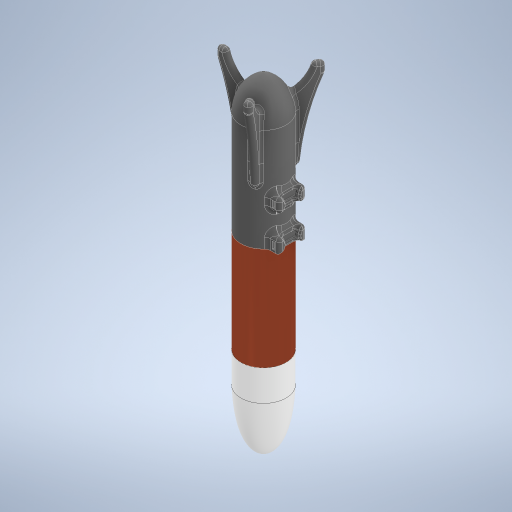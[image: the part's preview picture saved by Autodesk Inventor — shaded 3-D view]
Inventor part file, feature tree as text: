
AUTODESK INVENTOR PART (.ipt)
format: ipt  version: 2023 (Build 270158030, 158C)  size: 1,832,448 bytes
history: native  units: mm
features: fillet x17, sketch x15, extrude x14, other x12, plane x4, revolve x3, pattern_circular x2, pattern_linear x1, mirror x1, chamfer x1
ambient origin geometry x8: Origin, YZ Plane, XZ Plane, XY Plane, X Axis, Y Axis, Z Axis, Center Point
bodies: Body1 (feature_tree), Body2 (feature_tree), Body3 (feature_tree), Body4 (feature_tree), Body5 (feature_tree), Body6 (feature_tree), Body7 (feature_tree)
feature tree (70):
  other  "stage-one"
  extrude  "body-tube"  Depth=3.0mm
  extrude  "Extrusion2"  Depth=20.0mm
  extrude  "Extrusion3"  Depth=10.0mm
  plane  "Work Plane2"
  plane  "Work Plane4"
  extrude  "Extrusion4"  Depth=12.5mm
  plane  "Work Plane6"
  pattern_linear  "Rectangular Pattern1"  Count1=2  [1 undecoded]
  extrude  "Extrusion7"  Depth=6.0mm
  other  "Work Point2"
  revolve  "Revolution2"  [1 undecoded]
  mirror  "Mirror1"
  extrude  "Extrusion5"  Depth=4.0mm
  fillet  "Fillet1"  [1 undecoded]
  fillet  "Fillet2"  Radius=30.0mm
  fillet  "Fillet3"  Radius=200.0mm
  chamfer  "Chamfer1"  Distance=20.0mm
  fillet  "Fillet4"  Radius=7.0mm
  fillet  "Fillet5"  Radius=7.0mm
  fillet  "Fillet6"  Radius=5.0mm
  extrude  "Extrusion6"  Depth=2.0mm TaperAngle=45.0deg
  extrude  "fin 1 extrude"  Depth=5.0mm
  pattern_circular  "Circular Pattern1"  [2 undecoded]
  fillet  "Fillet7"  Radius=8.0mm
  fillet  "Fillet9"  Radius=10.0mm
  fillet  "Fillet10"  Radius=3.5mm
  fillet  "Fillet11"  [1 undecoded]
  fillet  "Fillet12"  Radius=1.0mm
  fillet  "Fillet13"  Radius=50.0mm
  extrude  "Extrusion9"  Depth=200.0mm
  extrude  "Extrusion10"  TaperAngle=90.0deg  [1 undecoded]
  extrude  "Extrusion11"  Depth=48.0mm
  extrude  "Extrusion12"  Depth=5.0mm
  other  "Work Point3"
  fillet  "Fillet15"  Radius=65.0mm
  fillet  "Fillet16"  Radius=15.0mm
  plane  "Work Plane7"
  extrude  "Extrusion14"  Depth=5.0mm
  revolve  "Revolution4"  [1 undecoded]
  fillet  "Fillet18"  Radius=126.0mm
  fillet  "Fillet19"  Radius=404.0mm
  fillet  "Fillet20"  Radius=150.0mm
  pattern_circular  "Circular Pattern2"  [2 undecoded]
  revolve  "Revolution3"  [1 undecoded]
  extrude  "Extrusion13"  Depth=5.0mm
  sketch  "Sketch1"  dims[d0=60.0mm d1=3.0mm]
  other  "rail-clamp-A"
  sketch  "Sketch5"  dims[d2=150.0mm d3=0.0mm d19=20.0mm]
  sketch  "Sketch6"  dims[d20=20.0mm d22=10.0mm]
  other  "Holding Bar"
  sketch  "Sketch8"  dims[d23=20.0mm d24=0.0mm d26=12.5mm]
  other  "bar-vertical"
  other  "Pattern of Holding Bar:1"
  other  "bar-angled"
  sketch  "Sketch9"  dims[d27=12.5mm]
  sketch  "Sketch10"  dims[d28=15.0mm]
  sketch  "Sketch11"  dims[d29=17.0mm]
  sketch  "Sketch12"  dims[d30=17.0mm]
  sketch  "Sketch13"  dims[d31=3.490659mm]
  sketch  "Sketch14"  dims[d33=3.490659mm]
  other  "stage-two"
  sketch  "Sketch15"  dims[d34=53.0mm d35=20.0mm]
  sketch  "Sketch16"  dims[d36=6.0mm d37=6.0mm]
  sketch  "Sketch17"  dims[d38=7.5mm d39=0.0mm d40=30.0mm]
  other  "nose-cone"
  sketch  "Sketch19"  dims[d41=53.296162mm d42=4.0mm]
  other  "drumsticks"
  sketch  "Sketch20"  dims[d43=200.0mm d44=100.0mm d45=0.0mm d46=0.0mm d47=90.0deg d49=30.0mm d50=200.0mm d51=100.0mm d52=0.0mm d53=0.0mm d56=20.0mm d58=50.0mm d59=7.0mm d60=7.0mm d61=5.0mm d62=2.0mm d63=2.0mm d64=45.0deg d65=5.0mm d66=5.0mm d67=8.0mm d68=10.0mm d70=3.5mm d76=0.0mm d77=0.0mm d78=1.0mm d79=50.0mm d80=0.0mm d85=53.0mm d86=52.992097mm d88=3.0mm d89=3.0mm d90=54.0mm d91=200.0mm d92=90.0deg d93=48.0mm d94=5.0mm d95=65.0mm d96=15.0mm d97=5.0mm d98=367.0mm d99=126.0mm d100=404.0mm d101=150.0mm d102=10.0mm d103=0.0mm d104=5.0mm d106=5.0mm d107=30.0mm d108=360.0deg d110=5.0mm d111=5.0mm d112=5.0mm d113=5.0mm d115=3.0mm d116=1.5mm d117=50.0mm d118=0.0mm d119=150.0mm d120=0.0mm d121=1.5mm d122=49.0mm d123=0.0mm d124=1.5mm d125=30.0mm d126=0.0mm d131=360.0deg d132=1.5mm d133=25.0mm d134=0.0mm d135=3.0mm d136=2.5mm d137=10.0mm d138=2.0mm d139=1.5mm d140=-110.0mm d141=15.0mm d142=400.0mm d143=0.0mm d144=15.0mm d145=0.0mm d147=19.0mm d148=15.0mm d149=410.0mm d150=7.5mm d151=13.0mm d152=10.5mm d153=2.25mm d154=2.25mm d159=3.85mm d160=3.85mm d161=50.0mm d162=2.0mm d163=50.0mm d164=339.5mm d165=360.0deg d166=5.0mm d167=3.0mm d168=10.0mm d169=80.0mm d170=360.0deg d184=3.0mm d189=128.5mm d190=4.8mm d191=3.35mm d192=30.0mm d193=28.0mm d194=7.0mm d195=7.0mm d196=45.0mm d197=75.0mm d198=78.0mm d200=1.5mm]
  other  "stick"
note: 11 required parameter values undecoded (feature->parameter linkage not recoverable at this tier; creation-order binding heuristic only, values carry confidence <= 0.55)